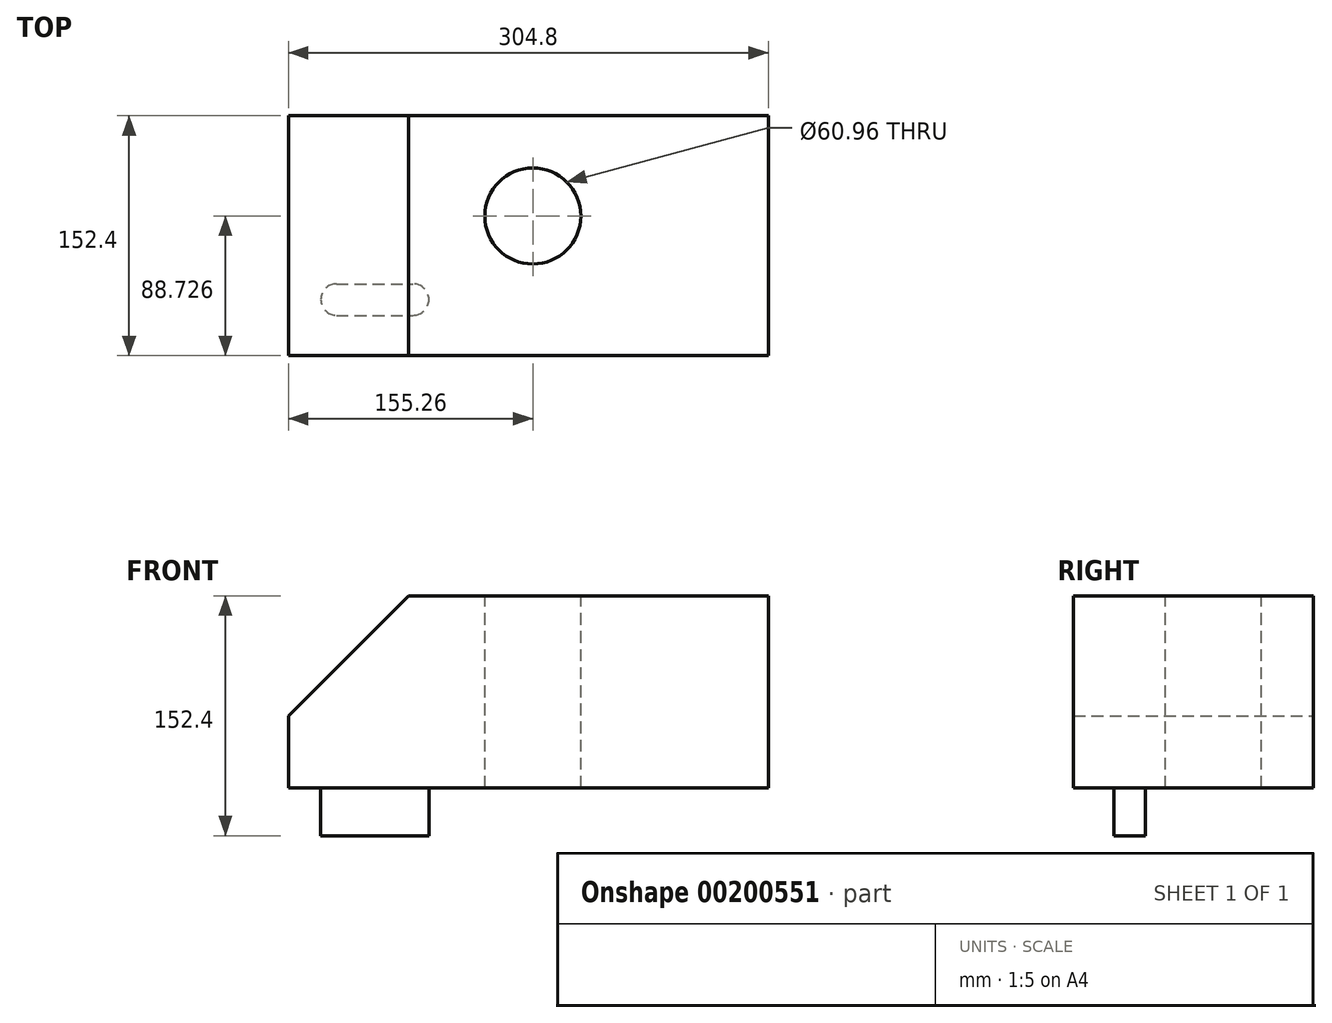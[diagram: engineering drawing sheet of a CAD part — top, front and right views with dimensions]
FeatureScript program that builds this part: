
annotation { "Feature Type Name" : "Feature", "Feature Type Description" : "" }
export const myFeature = defineFeature(function(context is Context, id is Id, definition is map)
    precondition{}
    {
        {
            var Q0;
            Q0=qCreatedBy(makeId("Top.planeOp"),FACE);
            var sketch = newSketch(context, id + "F0", { "sketchPlane" : qUnion([Q0])});
            skLineSegment(sketch, "E0.bottom", {"start": v(-155.26, 48.37) * mm, "end": v(149.54, 48.37) * mm});
            skLineSegment(sketch, "E0.top", {"start": v(-155.26, -104.03) * mm, "end": v(149.54, -104.03) * mm});
            skLineSegment(sketch, "E0.left", {"start": v(-155.26, 48.37) * mm, "end": v(-155.26, -104.03) * mm});
            skLineSegment(sketch, "E0.right", {"start": v(149.54, 48.37) * mm, "end": v(149.54, -104.03) * mm});
            skSolve(sketch);
        }
        {
            var Q0;
            Q0=makeQuery(id+"F0.imprint","IMPRINT",FACE,{"disambiguationData":[TD([[makeQuery(id+"F0.imprint","IMPRINT",EDGE,{"derivedFrom":sQuery(id+"F0.wireOp",EDGE,"E0.bottom")}),-1.0]])]});
            extrude(context, id + "F1", {"entities" : qUnion([Q0]), "depth" : 152.4 * mm});
        }
        {
            var Q0;
            Q0=makeQuery(id+"F1.opExtrude","CAP_FACE",FACE,{"disambiguationData":[OSD([sQuery(id+"F0.wireOp",EDGE,"E0.bottom"),sQuery(id+"F0.wireOp",EDGE,"E0.top"),sQuery(id+"F0.wireOp",EDGE,"E0.left"),sQuery(id+"F0.wireOp",EDGE,"E0.right")])],"isStart":false});
            var sketch = newSketch(context, id + "F2", { "sketchPlane" : qUnion([Q0])});
            skCircle(sketch, "E1", {"center": v(0, -27.09) * mm, "radius": 38.1 * mm});
            skSolve(sketch);
        }
        {
            var Q0;
            Q0=sQuery(id+"F2.wireOp",EDGE,"E1");
            extrude(context, id + "F3", {"bodyType" : ToolBodyType.SURFACE, "surfaceEntities" : qUnion([Q0]), "depth" : 914.4 * mm});
        }
        {
            var Q0;
            Q0=makeQuery(id+"F3.opExtrude","SWEPT_BODY",BODY,{"disambiguationData":[OSD([sQuery(id+"F2.wireOp",EDGE,"E1")])]});
            deleteBodies(context, id + "F4", {"entities" : qUnion([Q0])});
        }
        {
            var Q0;
            Q0=makeQuery(id+"F1.opExtrude","CAP_FACE",FACE,{"disambiguationData":[OSD([sQuery(id+"F0.wireOp",EDGE,"E0.bottom"),sQuery(id+"F0.wireOp",EDGE,"E0.top"),sQuery(id+"F0.wireOp",EDGE,"E0.left"),sQuery(id+"F0.wireOp",EDGE,"E0.right")])],"isStart":false});
            var sketch = newSketch(context, id + "F9", { "sketchPlane" : qUnion([Q0])});
            skCircle(sketch, "E2", {"center": v(0, -15.3) * mm, "radius": 30.48 * mm});
            skSolve(sketch);
        }
        {
            var Q0;
            Q0=makeQuery(id+"F9.imprint","IMPRINT",FACE,{"disambiguationData":[TD([[makeQuery(id+"F9.imprint","IMPRINT",EDGE,{"derivedFrom":sQuery(id+"F9.wireOp",EDGE,"E2")}),1.0]])]});
            var Q1;
            Q1=sQuery(id+"F9.wireOp",EDGE,"E2");
            extrude(context, id + "F5", {"entities" : qUnion([Q0]), "operationType" : NewBodyOperationType.REMOVE, "surfaceEntities" : qUnion([Q1]), "endBound" : BoundingType.THROUGH_ALL, "oppositeDirection" : true, "depth" : 30.48 * mm});
        }
        {
            var Q0;
            Q0=makeQuery(id+"F1.opExtrude","CAP_EDGE",EDGE,{"disambiguationData":[OSD([sQuery(id+"F0.wireOp",EDGE,"E0.left")])],"isStart":false});
            chamfer(context, id + "F6", {"entities" : qUnion([Q0]), "width" : 76.2 * mm, "tangentPropagation" : true});
        }
        {
            var Q0;
            Q0=makeQuery(id+"F1.opExtrude","CAP_FACE",FACE,{"disambiguationData":[OSD([sQuery(id+"F0.wireOp",EDGE,"E0.bottom"),sQuery(id+"F0.wireOp",EDGE,"E0.top"),sQuery(id+"F0.wireOp",EDGE,"E0.left"),sQuery(id+"F0.wireOp",EDGE,"E0.right")])],"isStart":true});
            var sketch = newSketch(context, id + "F7", { "sketchPlane" : qUnion([Q0])});
            skLineSegment(sketch, "E3", {"start": v(-124.65, 68.4) * mm, "end": v(-75.99, 68.4) * mm, "construction": true});
            skArc(sketch, "E4.0.startCap", {"start": v(-124.65, 58.4) * mm, "mid": v(-134.65, 68.4) * mm, "end": v(-124.65, 78.4) * mm});
            skArc(sketch, "E4.0.endCap", {"start": v(-75.99, 78.4) * mm, "mid": v(-65.99, 68.4) * mm, "end": v(-75.99, 58.4) * mm});
            skLineSegment(sketch, "E4.0.left", {"start": v(-124.65, 78.4) * mm, "end": v(-75.99, 78.4) * mm});
            skLineSegment(sketch, "E4.0.right", {"start": v(-124.65, 58.4) * mm, "end": v(-75.99, 58.4) * mm});
            skSolve(sketch);
        }
        {
            var Q0;
            Q0=makeQuery(id+"F7.imprint","IMPRINT",FACE,{"disambiguationData":[TD([[makeQuery(id+"F7.imprint","IMPRINT",EDGE,{"derivedFrom":sQuery(id+"F7.wireOp",EDGE,"E4.0.startCap")}),-1.0]])]});
            extrude(context, id + "F8", {"entities" : qUnion([Q0]), "operationType" : NewBodyOperationType.REMOVE, "oppositeDirection" : true, "depth" : 30.48 * mm});
        }
    });
